# Revit family: Mailboxes_4C-Salsbury_Industries-Front_Load-Max_Height_Units
name_source: partatom
category: Specialty Equipment
revit_build: Autodesk Revit 2016 (Build: 20190507_1515(x64)
units: mm (PartAtom-declared; Revit-internal decimal feet)

## family parameters
Cut with Voids When Loaded = No
Host = Face
OmniClass Number = 23.40.90.14.11
OmniClass Title = Mail Boxes
Part Type = Normal
Room Calculation Point = No
Round Connector Dimension = Use Diameter
Shared = No

## types (12) — shared parameters
Assembly Code = C1030910
Assembly Description = Mailboxes
Back Enclosure Material = Aluminum Alloy - Salsbury Finish - Clear (No finish)
Center Divider Offset = 14.381"
Decals = Polycarbonate Film - Salsbury Finish - White
Depth = 16.450"
Door Depth = 0.190"
Height = 57.140"
Lock Material = Stainless Steel - Salsbury Finish -  Polished
Manufacturer = Salsbury Industries
MasterFormat Number = 10 55 00
MasterFormat Title = Postal Specialties
OmniClass 23 Number = 23.40.90.14.11
OmniClass 23 Title = Mail Boxes
Rough Opening - Height = 55.875"
URL = www.mailboxes.com
Version = 5.0 (01/01/21)

## per-type parameters (varying)
- 3716D-8P FL: Bottom Back Plate=Yes; Center Extrusion Offset=0.000"; Description=Max Height Unit: 2 PL3, 4 PL4, 2 PL4.5; Door Slot L1=3700 Series 4C Door Configurations : Empty; Door Slot L10=3700 Series 4C Door Configurations : Empty; Door Slot L10.5=3700 Series 4C Door Configurations : Empty; Door Slot L11=3700 Series 4C Parcel Configurations : PL4 w/ Divider; Door Slot L11.5=3700 Series 4C Door Configurations : Empty; Door Slot L12.5=3700 Series 4C Door Configurations : Empty; Door Slot L13.5=3700 Series 4C Door Configurations : Empty; Door Slot L16=3700 Series 4C Parcel Configurations : PL4.5 w/ Divider; Door Slot L2=3700 Series 4C Door Configurations : Empty; Door Slot L3=3700 Series 4C Parcel Configurations : PL3; Door Slot L4=3700 Series 4C Door Configurations : Empty; Door Slot L5=3700 Series 4C Door Configurations : Empty; Door Slot L6=3700 Series 4C Door Configurations : Empty; Door Slot L6.5=3700 Series 4C Door Configurations : Empty; Door Slot L7=3700 Series 4C Parcel Configurations : PL4 w/ Divider; Door Slot L7.5=3700 Series 4C Door Configurations : Empty; Door Slot L8=3700 Series 4C Door Configurations : Empty; Door Slot L8.5=3700 Series 4C Door Configurations : Empty; Door Slot L9=3700 Series 4C Door Configurations : Empty; Door Slot L9.5=3700 Series 4C Door Configurations : Empty; Door Slot R1=3700 Series 4C Door Configurations : Empty; Door Slot R10=3700 Series 4C Door Configurations : Empty; Door Slot R10.5=3700 Series 4C Door Configurations : Empty; Door Slot R11=3700 Series 4C Parcel Configurations : PL4 w/ Divider; Door Slot R11.5=3700 Series 4C Door Configurations : Empty; Door Slot R12.5=3700 Series 4C Door Configurations : Empty; Door Slot R13.5=3700 Series 4C Door Configurations : Empty; Door Slot R16=3700 Series 4C Parcel Configurations : PL4.5 w/ Divider; Door Slot R2=3700 Series 4C Door Configurations : Empty; Door Slot R3=3700 Series 4C Parcel Configurations : PL3; Door Slot R4=3700 Series 4C Door Configurations : Empty; Door Slot R5=3700 Series 4C Door Configurations : Empty; Door Slot R6=3700 Series 4C Door Configurations : Empty; Door Slot R6.5=3700 Series 4C Door Configurations : Empty; Door Slot R7=3700 Series 4C Parcel Configurations : PL4 w/ Divider; Door Slot R7.5=3700 Series 4C Door Configurations : Empty; Door Slot R8=3700 Series 4C Door Configurations : Empty; Door Slot R8.5=3700 Series 4C Door Configurations : Empty; Door Slot R9=3700 Series 4C Door Configurations : Empty; Door Slot R9.5=3700 Series 4C Door Configurations : Empty; Door Spacer=3700 Series 4C Door Configurations : Empty; Double Wide Hidden Components=Yes; Left Inside Wall=Yes; Right Inside Wall=Yes; Rough Opening - Width=29.875"; Top Back Plate=Yes; Type Comments=4C Standard Horizontal Mailbox - Front Loading; Vertical Center Divider=Yes; Width=31.097"
- 3716D-20 FL: Bottom Back Plate=Yes; Center Extrusion Offset=0.000"; Description=Max Height Unit: 20 MB1, 2 PL4.5, OM2; Door Slot L1=3700 Series 4C Door Configurations : MB1 Door; Door Slot L10=3700 Series 4C Door Configurations : MB1 Door w/ Divider; Door Slot L10.5=3700 Series 4C Door Configurations : Empty; Door Slot L11=3700 Series 4C Door Configurations : MB1 Door w/ Divider; Door Slot L11.5=3700 Series 4C Door Configurations : Empty; Door Slot L12.5=3700 Series 4C Door Configurations : Empty; Door Slot L13.5=3700 Series 4C Door Configurations : Empty; Door Slot L16=3700 Series 4C Parcel Configurations : PL4.5 w/ Divider; Door Slot L2=3700 Series 4C Door Configurations : MB1 Door w/ Divider; Door Slot L3=3700 Series 4C Door Configurations : MB1 Door w/ Divider; Door Slot L4=3700 Series 4C Door Configurations : MB1 Door w/ Divider; Door Slot L5=3700 Series 4C Door Configurations : MB1 Door w/ Divider; Door Slot L6=3700 Series 4C Door Configurations : MB1 Door w/ Divider; Door Slot L6.5=3700 Series 4C Door Configurations : Empty; Door Slot L7=3700 Series 4C Door Configurations : MB1 Door w/ Divider; Door Slot L7.5=3700 Series 4C Door Configurations : Empty; Door Slot L8=3700 Series 4C Door Configurations : MB1 Door w/ Divider; Door Slot L8.5=3700 Series 4C Door Configurations : Empty; Door Slot L9=3700 Series 4C Door Configurations : MB1 Door w/ Divider; Door Slot L9.5=3700 Series 4C Door Configurations : Empty; Door Slot R1=3700 Series 4C Door Configurations : MB1 Door; Door Slot R10=3700 Series 4C Door Configurations : MB1 Door w/ Divider; Door Slot R10.5=3700 Series 4C Door Configurations : Empty; Door Slot R11=3700 Series 4C Door Configurations : MB1 Door w/ Divider; Door Slot R11.5=3700 Series 4C Door Configurations : Empty; Door Slot R12.5=3700 Series 4C Door Configurations : Empty; Door Slot R13.5=3700 Series 4C Door Configurations : Empty; Door Slot R16=3700 Series 4C Parcel Configurations : PL4.5 w/ Divider; Door Slot R2=3700 Series 4C Door Configurations : MB1 Door w/ Divider; Door Slot R3=3700 Series 4C Door Configurations : MB1 Door w/ Divider; Door Slot R4=3700 Series 4C Door Configurations : MB1 Door w/ Divider; Door Slot R5=3700 Series 4C Door Configurations : MB1 Door w/ Divider; Door Slot R6=3700 Series 4C Door Configurations : MB1 Door w/ Divider; Door Slot R6.5=3700 Series 4C Door Configurations : Empty; Door Slot R7=3700 Series 4C Door Configurations : Empty; Door Slot R7.5=3700 Series 4C Door Configurations : Empty; Door Slot R8=3700 Series 4C OM2 Configuration : OM2-FL; Door Slot R8.5=3700 Series 4C Door Configurations : Empty; Door Slot R9=3700 Series 4C Door Configurations : MB1 Door w/ Divider; Door Slot R9.5=3700 Series 4C Door Configurations : Empty; Door Spacer=3700 Series 4C Door Configurations : Empty; Double Wide Hidden Components=Yes; Left Inside Wall=Yes; Right Inside Wall=Yes; Rough Opening - Width=29.875"; Top Back Plate=Yes; Type Comments=4C Standard Horizontal Mailbox - Front Loading; Vertical Center Divider=Yes; Width=31.097"
- 3716D-29 FL: Bottom Back Plate=Yes; Center Extrusion Offset=0.000"; Description=Max Height Unit: 29 MB1, OM1.5; Door Slot L1=3700 Series 4C Door Configurations : MB1 Door; Door Slot L10=3700 Series 4C Door Configurations : Empty; Door Slot L10.5=3700 Series 4C Door Configurations : MB1 Door w/ Divider; Door Slot L11=3700 Series 4C Door Configurations : Empty; Door Slot L11.5=3700 Series 4C Door Configurations : MB1 Door w/ Divider; Door Slot L12.5=3700 Series 4C Door Configurations : MB1 Door w/ Divider; Door Slot L13.5=3700 Series 4C Door Configurations : MB1 Door w/ Divider; Door Slot L16=3700 Series 4C Door Configurations : MB1 Door w/ Divider; Door Slot L2=3700 Series 4C Door Configurations : MB1 Door w/ Divider; Door Slot L3=3700 Series 4C Door Configurations : MB1 Door w/ Divider; Door Slot L4=3700 Series 4C Door Configurations : MB1 Door w/ Divider; Door Slot L5=3700 Series 4C Door Configurations : MB1 Door w/ Divider; Door Slot L6=3700 Series 4C Door Configurations : MB1 Door w/ Divider; Door Slot L6.5=3700 Series 4C Door Configurations : MB1 Door w/ Divider; Door Slot L7=3700 Series 4C Door Configurations : Empty; Door Slot L7.5=3700 Series 4C Door Configurations : MB1 Door w/ Divider; Door Slot L8=3700 Series 4C Door Configurations : Empty; Door Slot L8.5=3700 Series 4C Door Configurations : MB1 Door w/ Divider; Door Slot L9=3700 Series 4C Door Configurations : Empty; Door Slot L9.5=3700 Series 4C Door Configurations : MB1 Door w/ Divider; Door Slot R1=3700 Series 4C Door Configurations : MB1 Door; Door Slot R10=3700 Series 4C Door Configurations : Empty; Door Slot R10.5=3700 Series 4C Door Configurations : MB1 Door w/ Divider; Door Slot R11=3700 Series 4C Door Configurations : Empty; Door Slot R11.5=3700 Series 4C Door Configurations : MB1 Door w/ Divider; Door Slot R12.5=3700 Series 4C Door Configurations : MB1 Door w/ Divider; Door Slot R13.5=3700 Series 4C Door Configurations : MB1 Door w/ Divider; Door Slot R16=3700 Series 4C Door Configurations : MB1 Door w/ Divider; Door Slot R2=3700 Series 4C Door Configurations : MB1 Door w/ Divider; Door Slot R3=3700 Series 4C Door Configurations : MB1 Door w/ Divider; Door Slot R4=3700 Series 4C Door Configurations : MB1 Door w/ Divider; Door Slot R5=3700 Series 4C Door Configurations : MB1 Door w/ Divider; Door Slot R6=3700 Series 4C Door Configurations : MB1 Door w/ Divider; Door Slot R6.5=3700 Series 4C OM1.5 Configuration : OM1.5-FL; Door Slot R7=3700 Series 4C Door Configurations : Empty; Door Slot R7.5=3700 Series 4C Door Configurations : MB1 Door w/ Divider; Door Slot R8=3700 Series 4C Door Configurations : Empty; Door Slot R8.5=3700 Series 4C Door Configurations : MB1 Door w/ Divider; Door Slot R9=3700 Series 4C Door Configurations : Empty; Door Slot R9.5=3700 Series 4C Door Configurations : MB1 Door w/ Divider; Door Spacer=3700 Series 4C Door Spacing Filler : Door Space Filler; Double Wide Hidden Components=Yes; Left Inside Wall=Yes; Right Inside Wall=Yes; Rough Opening - Width=29.875"; Top Back Plate=Yes; Type Comments=4C Standard Horizontal Mailbox - Front Loading; Vertical Center Divider=Yes; Width=31.097"
- 3716S-06 FL: Bottom Back Plate=No; Center Extrusion Offset=0.350"; Description=Max Height Unit: 6 MB1, 1 PL3, 1 PL4.5, OM2; Door Slot L1=3700 Series 4C Door Configurations : Empty; Door Slot L10=3700 Series 4C Door Configurations : Empty; Door Slot L10.5=3700 Series 4C Door Configurations : Empty; Door Slot L11=3700 Series 4C Door Configurations : Empty; Door Slot L11.5=3700 Series 4C Door Configurations : Empty; Door Slot L12.5=3700 Series 4C Door Configurations : Empty; Door Slot L13.5=3700 Series 4C Door Configurations : Empty; Door Slot L16=3700 Series 4C Door Configurations : Empty; Door Slot L2=3700 Series 4C Door Configurations : Empty; Door Slot L3=3700 Series 4C Door Configurations : Empty; Door Slot L4=3700 Series 4C Door Configurations : Empty; Door Slot L5=3700 Series 4C Door Configurations : Empty; Door Slot L6=3700 Series 4C Door Configurations : Empty; Door Slot L6.5=3700 Series 4C Door Configurations : Empty; Door Slot L7=3700 Series 4C Door Configurations : Empty; Door Slot L7.5=3700 Series 4C Door Configurations : Empty; Door Slot L8=3700 Series 4C Door Configurations : Empty; Door Slot L8.5=3700 Series 4C Door Configurations : Empty; Door Slot L9=3700 Series 4C Door Configurations : Empty; Door Slot L9.5=3700 Series 4C Door Configurations : Empty; Door Slot R1=3700 Series 4C Door Configurations : MB1 Door; Door Slot R10=3700 Series 4C Door Configurations : Empty; Door Slot R10.5=3700 Series 4C Door Configurations : Empty; Door Slot R11=3700 Series 4C Parcel Configurations : PL3 w/ Divider; Door Slot R11.5=3700 Series 4C Door Configurations : Empty; Door Slot R12.5=3700 Series 4C Door Configurations : Empty; Door Slot R13.5=3700 Series 4C Door Configurations : Empty; Door Slot R16=3700 Series 4C Parcel Configurations : PL4.5 w/ Divider; Door Slot R2=3700 Series 4C Door Configurations : MB1 Door w/ Divider; Door Slot R3=3700 Series 4C Door Configurations : MB1 Door w/ Divider; Door Slot R4=3700 Series 4C Door Configurations : MB1 Door w/ Divider; Door Slot R5=3700 Series 4C Door Configurations : MB1 Door w/ Divider; Door Slot R6=3700 Series 4C Door Configurations : MB1 Door w/ Divider; Door Slot R6.5=3700 Series 4C Door Configurations : Empty; Door Slot R7=3700 Series 4C Door Configurations : Empty; Door Slot R7.5=3700 Series 4C Door Configurations : Empty; Door Slot R8=3700 Series 4C OM2 Configuration : OM2-FL; Door Slot R8.5=3700 Series 4C Door Configurations : Empty; Door Slot R9=3700 Series 4C Door Configurations : Empty; Door Slot R9.5=3700 Series 4C Door Configurations : Empty; Door Spacer=3700 Series 4C Door Configurations : Empty; Double Wide Hidden Components=No; Left Inside Wall=No; Right Inside Wall=No; Rough Opening - Width=15.750"; Top Back Plate=No; Type Comments=4C Standard Horizontal Mailbox - Front Loading; Vertical Center Divider=No; Width=16.966"
- 3716S-3P FL: Bottom Back Plate=No; Center Extrusion Offset=0.350"; Description=Max Height Unit: 1 PL4.5, 1 PL5, 1 PL6; Door Slot L1=3700 Series 4C Door Configurations : Empty; Door Slot L10=3700 Series 4C Door Configurations : Empty; Door Slot L10.5=3700 Series 4C Door Configurations : Empty; Door Slot L11=3700 Series 4C Door Configurations : Empty; Door Slot L11.5=3700 Series 4C Door Configurations : Empty; Door Slot L12.5=3700 Series 4C Door Configurations : Empty; Door Slot L13.5=3700 Series 4C Door Configurations : Empty; Door Slot L16=3700 Series 4C Door Configurations : Empty; Door Slot L2=3700 Series 4C Door Configurations : Empty; Door Slot L3=3700 Series 4C Door Configurations : Empty; Door Slot L4=3700 Series 4C Door Configurations : Empty; Door Slot L5=3700 Series 4C Door Configurations : Empty; Door Slot L6=3700 Series 4C Door Configurations : Empty; Door Slot L6.5=3700 Series 4C Door Configurations : Empty; Door Slot L7=3700 Series 4C Door Configurations : Empty; Door Slot L7.5=3700 Series 4C Door Configurations : Empty; Door Slot L8=3700 Series 4C Door Configurations : Empty; Door Slot L8.5=3700 Series 4C Door Configurations : Empty; Door Slot L9=3700 Series 4C Door Configurations : Empty; Door Slot L9.5=3700 Series 4C Door Configurations : Empty; Door Slot R1=3700 Series 4C Door Configurations : Empty; Door Slot R10=3700 Series 4C Door Configurations : Empty; Door Slot R10.5=3700 Series 4C Door Configurations : Empty; Door Slot R11=3700 Series 4C Parcel Configurations : PL6 w/ Divider; Door Slot R11.5=3700 Series 4C Door Configurations : Empty; Door Slot R12.5=3700 Series 4C Door Configurations : Empty; Door Slot R13.5=3700 Series 4C Door Configurations : Empty; Door Slot R16=3700 Series 4C Parcel Configurations : PL4.5 w/ Divider; Door Slot R2=3700 Series 4C Door Configurations : Empty; Door Slot R3=3700 Series 4C Door Configurations : Empty; Door Slot R4=3700 Series 4C Door Configurations : Empty; Door Slot R5=3700 Series 4C Parcel Configurations : PL5; Door Slot R6=3700 Series 4C Door Configurations : Empty; Door Slot R6.5=3700 Series 4C Door Configurations : Empty; Door Slot R7=3700 Series 4C Door Configurations : Empty; Door Slot R7.5=3700 Series 4C Door Configurations : Empty; Door Slot R8=3700 Series 4C Door Configurations : Empty; Door Slot R8.5=3700 Series 4C Door Configurations : Empty; Door Slot R9=3700 Series 4C Door Configurations : Empty; Door Slot R9.5=3700 Series 4C Door Configurations : Empty; Door Spacer=3700 Series 4C Door Configurations : Empty; Double Wide Hidden Components=No; Left Inside Wall=No; Right Inside Wall=No; Rough Opening - Width=15.750"; Top Back Plate=No; Type Comments=4C Standard Horizontal Mailbox - Front Loading; Vertical Center Divider=No; Width=16.966"
- 3716S-14 FL: Bottom Back Plate=No; Center Extrusion Offset=0.350"; Description=Max Height Unit: 14 MB1, OM2; Door Slot L1=3700 Series 4C Door Configurations : Empty; Door Slot L10=3700 Series 4C Door Configurations : Empty; Door Slot L10.5=3700 Series 4C Door Configurations : Empty; Door Slot L11=3700 Series 4C Door Configurations : Empty; Door Slot L11.5=3700 Series 4C Door Configurations : Empty; Door Slot L12.5=3700 Series 4C Door Configurations : Empty; Door Slot L13.5=3700 Series 4C Door Configurations : Empty; Door Slot L16=3700 Series 4C Door Configurations : Empty; Door Slot L2=3700 Series 4C Door Configurations : Empty; Door Slot L3=3700 Series 4C Door Configurations : Empty; Door Slot L4=3700 Series 4C Door Configurations : Empty; Door Slot L5=3700 Series 4C Door Configurations : Empty; Door Slot L6=3700 Series 4C Door Configurations : Empty; Door Slot L6.5=3700 Series 4C Door Configurations : Empty; Door Slot L7=3700 Series 4C Door Configurations : Empty; Door Slot L7.5=3700 Series 4C Door Configurations : Empty; Door Slot L8=3700 Series 4C Door Configurations : Empty; Door Slot L8.5=3700 Series 4C Door Configurations : Empty; Door Slot L9=3700 Series 4C Door Configurations : Empty; Door Slot L9.5=3700 Series 4C Door Configurations : Empty; Door Slot R1=3700 Series 4C Door Configurations : MB1 Door; Door Slot R10=3700 Series 4C Door Configurations : Empty; Door Slot R10.5=3700 Series 4C Door Configurations : MB1 Door w/ Divider; Door Slot R11=3700 Series 4C Door Configurations : Empty; Door Slot R11.5=3700 Series 4C Door Configurations : MB1 Door w/ Divider; Door Slot R12.5=3700 Series 4C Door Configurations : MB1 Door w/ Divider; Door Slot R13.5=3700 Series 4C Door Configurations : MB1 Door w/ Divider; Door Slot R16=3700 Series 4C Door Configurations : MB1 Door w/ Divider; Door Slot R2=3700 Series 4C Door Configurations : MB1 Door w/ Divider; Door Slot R3=3700 Series 4C Door Configurations : MB1 Door w/ Divider; Door Slot R4=3700 Series 4C Door Configurations : MB1 Door w/ Divider; Door Slot R5=3700 Series 4C Door Configurations : MB1 Door w/ Divider; Door Slot R6=3700 Series 4C Door Configurations : MB1 Door w/ Divider; Door Slot R6.5=3700 Series 4C OM1.5 Configuration : OM1.5-FL; Door Slot R7=3700 Series 4C Door Configurations : Empty; Door Slot R7.5=3700 Series 4C Door Configurations : MB1 Door w/ Divider; Door Slot R8=3700 Series 4C Door Configurations : Empty; Door Slot R8.5=3700 Series 4C Door Configurations : MB1 Door w/ Divider; Door Slot R9=3700 Series 4C Door Configurations : Empty; Door Slot R9.5=3700 Series 4C Door Configurations : MB1 Door w/ Divider; Door Spacer=3700 Series 4C Door Configurations : Empty; Double Wide Hidden Components=No; Left Inside Wall=No; Right Inside Wall=No; Rough Opening - Width=15.750"; Top Back Plate=No; Type Comments=4C Standard Horizontal Mailbox - Front Loading; Vertical Center Divider=No; Width=16.966"
- 3716S-09 FL: Bottom Back Plate=No; Center Extrusion Offset=0.350"; Description=Max Height Unit: 9 MB1, 1 PL4.5, OM2; Door Slot L1=3700 Series 4C Door Configurations : Empty; Door Slot L10=3700 Series 4C Door Configurations : Empty; Door Slot L10.5=3700 Series 4C Door Configurations : Empty; Door Slot L11=3700 Series 4C Door Configurations : Empty; Door Slot L11.5=3700 Series 4C Door Configurations : Empty; Door Slot L12.5=3700 Series 4C Door Configurations : Empty; Door Slot L13.5=3700 Series 4C Door Configurations : Empty; Door Slot L16=3700 Series 4C Door Configurations : Empty; Door Slot L2=3700 Series 4C Door Configurations : Empty; Door Slot L3=3700 Series 4C Door Configurations : Empty; Door Slot L4=3700 Series 4C Door Configurations : Empty; Door Slot L5=3700 Series 4C Door Configurations : Empty; Door Slot L6=3700 Series 4C Door Configurations : Empty; Door Slot L6.5=3700 Series 4C Door Configurations : Empty; Door Slot L7=3700 Series 4C Door Configurations : Empty; Door Slot L7.5=3700 Series 4C Door Configurations : Empty; Door Slot L8=3700 Series 4C Door Configurations : Empty; Door Slot L8.5=3700 Series 4C Door Configurations : Empty; Door Slot L9=3700 Series 4C Door Configurations : Empty; Door Slot L9.5=3700 Series 4C Door Configurations : Empty; Door Slot R1=3700 Series 4C Door Configurations : MB1 Door; Door Slot R10=3700 Series 4C Door Configurations : MB1 Door w/ Divider; Door Slot R10.5=3700 Series 4C Door Configurations : Empty; Door Slot R11=3700 Series 4C Door Configurations : MB1 Door w/ Divider; Door Slot R11.5=3700 Series 4C Door Configurations : Empty; Door Slot R12.5=3700 Series 4C Door Configurations : Empty; Door Slot R13.5=3700 Series 4C Door Configurations : Empty; Door Slot R16=3700 Series 4C Parcel Configurations : PL4.5 w/ Divider; Door Slot R2=3700 Series 4C Door Configurations : MB1 Door w/ Divider; Door Slot R3=3700 Series 4C Door Configurations : MB1 Door w/ Divider; Door Slot R4=3700 Series 4C Door Configurations : MB1 Door w/ Divider; Door Slot R5=3700 Series 4C Door Configurations : MB1 Door w/ Divider; Door Slot R6=3700 Series 4C Door Configurations : MB1 Door w/ Divider; Door Slot R6.5=3700 Series 4C Door Configurations : Empty; Door Slot R7=3700 Series 4C Door Configurations : Empty; Door Slot R7.5=3700 Series 4C Door Configurations : Empty; Door Slot R8=3700 Series 4C OM2 Configuration : OM2-FL; Door Slot R8.5=3700 Series 4C Door Configurations : Empty; Door Slot R9=3700 Series 4C Door Configurations : MB1 Door w/ Divider; Door Slot R9.5=3700 Series 4C Door Configurations : Empty; Door Spacer=3700 Series 4C Door Configurations : Empty; Double Wide Hidden Components=No; Left Inside Wall=No; Right Inside Wall=No; Rough Opening - Width=15.750"; Top Back Plate=No; Type Comments=4C Standard Horizontal Mailbox - Front Loading; Vertical Center Divider=No; Width=16.966"
- 3716S-2B FL: Bottom Back Plate=No; Center Extrusion Offset=0.350"; Description=Max Height Unit: 2 Receptacles; Door Slot L1=3700 Series 4C Door Configurations : Empty; Door Slot L10=3700 Series 4C Door Configurations : Empty; Door Slot L10.5=3700 Series 4C Door Configurations : Empty; Door Slot L11=3700 Series 4C Door Configurations : Empty; Door Slot L11.5=3700 Series 4C Door Configurations : Empty; Door Slot L12.5=3700 Series 4C Door Configurations : Empty; Door Slot L13.5=3700 Series 4C Door Configurations : Empty; Door Slot L16=3700 Series 4C Door Configurations : Empty; Door Slot L2=3700 Series 4C Door Configurations : Empty; Door Slot L3=3700 Series 4C Door Configurations : Empty; Door Slot L4=3700 Series 4C Door Configurations : Empty; Door Slot L5=3700 Series 4C Door Configurations : Empty; Door Slot L6=3700 Series 4C Door Configurations : Empty; Door Slot L6.5=3700 Series 4C Door Configurations : Empty; Door Slot L7=3700 Series 4C Door Configurations : Empty; Door Slot L7.5=3700 Series 4C Door Configurations : Empty; Door Slot L8=3700 Series 4C Door Configurations : Empty; Door Slot L8.5=3700 Series 4C Door Configurations : Empty; Door Slot L9=3700 Series 4C Door Configurations : Empty; Door Slot L9.5=3700 Series 4C Door Configurations : Empty; Door Slot R1=3700 Series 4C Door Configurations : Empty; Door Slot R10=3700 Series 4C Door Configurations : Empty; Door Slot R10.5=3700 Series 4C Door Configurations : Empty; Door Slot R11=3700 Series 4C Door Configurations : Empty; Door Slot R11.5=3700 Series 4C Door Configurations : Empty; Door Slot R12.5=3700 Series 4C Door Configurations : Empty; Door Slot R13.5=3700 Series 4C Door Configurations : Empty; Door Slot R16=4C-Max Height Receptacle; Door Slot R2=3700 Series 4C Door Configurations : Empty; Door Slot R3=3700 Series 4C Door Configurations : Empty; Door Slot R4=3700 Series 4C Door Configurations : Empty; Door Slot R5=3700 Series 4C Door Configurations : Empty; Door Slot R6=3700 Series 4C Door Configurations : Empty; Door Slot R6.5=3700 Series 4C Door Configurations : Empty; Door Slot R7=3700 Series 4C Door Configurations : Empty; Door Slot R7.5=3700 Series 4C Door Configurations : Empty; Door Slot R8=3700 Series 4C Door Configurations : Empty; Door Slot R8.5=3700 Series 4C Door Configurations : Empty; Door Slot R9=3700 Series 4C Door Configurations : Empty; Door Slot R9.5=3700 Series 4C Door Configurations : Empty; Door Spacer=3700 Series 4C Door Configurations : Empty; Double Wide Hidden Components=No; Left Inside Wall=No; Right Inside Wall=No; Rough Opening - Width=15.750"; Top Back Plate=No; Type Comments=4C Standard Horizontal Receptacle - Front Loading; Vertical Center Divider=No; Width=16.966"
- 3716S-1C FL: Bottom Back Plate=No; Center Extrusion Offset=0.350"; Description=Max Height Unit: 1 Collection Box; Door Slot L1=3700 Series 4C Door Configurations : Empty; Door Slot L10=3700 Series 4C Door Configurations : Empty; Door Slot L10.5=3700 Series 4C Door Configurations : Empty; Door Slot L11=3700 Series 4C Door Configurations : Empty; Door Slot L11.5=3700 Series 4C Door Configurations : Empty; Door Slot L12.5=3700 Series 4C Door Configurations : Empty; Door Slot L13.5=3700 Series 4C Door Configurations : Empty; Door Slot L16=3700 Series 4C Door Configurations : Empty; Door Slot L2=3700 Series 4C Door Configurations : Empty; Door Slot L3=3700 Series 4C Door Configurations : Empty; Door Slot L4=3700 Series 4C Door Configurations : Empty; Door Slot L5=3700 Series 4C Door Configurations : Empty; Door Slot L6=3700 Series 4C Door Configurations : Empty; Door Slot L6.5=3700 Series 4C Door Configurations : Empty; Door Slot L7=3700 Series 4C Door Configurations : Empty; Door Slot L7.5=3700 Series 4C Door Configurations : Empty; Door Slot L8=3700 Series 4C Door Configurations : Empty; Door Slot L8.5=3700 Series 4C Door Configurations : Empty; Door Slot L9=3700 Series 4C Door Configurations : Empty; Door Slot L9.5=3700 Series 4C Door Configurations : Empty; Door Slot R1=3700 Series 4C Door Configurations : Empty; Door Slot R10=3700 Series 4C Door Configurations : Empty; Door Slot R10.5=3700 Series 4C Door Configurations : Empty; Door Slot R11=3700 Series 4C Door Configurations : Empty; Door Slot R11.5=3700 Series 4C Door Configurations : Empty; Door Slot R12.5=3700 Series 4C Door Configurations : Empty; Door Slot R13.5=3700 Series 4C Door Configurations : Empty; Door Slot R16=4C-Max Height Collection Box; Door Slot R2=3700 Series 4C Door Configurations : Empty; Door Slot R3=3700 Series 4C Door Configurations : Empty; Door Slot R4=3700 Series 4C Door Configurations : Empty; Door Slot R5=3700 Series 4C Door Configurations : Empty; Door Slot R6=3700 Series 4C Door Configurations : Empty; Door Slot R6.5=3700 Series 4C Door Configurations : Empty; Door Slot R7=3700 Series 4C Door Configurations : Empty; Door Slot R7.5=3700 Series 4C Door Configurations : Empty; Door Slot R8=3700 Series 4C Door Configurations : Empty; Door Slot R8.5=3700 Series 4C Door Configurations : Empty; Door Slot R9=3700 Series 4C Door Configurations : Empty; Door Slot R9.5=3700 Series 4C Door Configurations : Empty; Door Spacer=3700 Series 4C Door Configurations : Empty; Double Wide Hidden Components=No; Left Inside Wall=No; Right Inside Wall=No; Rough Opening - Width=15.750"; Top Back Plate=No; Type Comments=4C Standard Horizontal Receptacle - Front Loading; Vertical Center Divider=No; Width=16.966"
- 3716D-15 FL: Bottom Back Plate=Yes; Center Extrusion Offset=0.000"; Description=Max Height Unit: 15 MB1, 2 PL4.5, 1 PL5, OM2; Door Slot L1=3700 Series 4C Door Configurations : MB1 Door; Door Slot L10=3700 Series 4C Door Configurations : Empty; Door Slot L10.5=3700 Series 4C Door Configurations : Empty; Door Slot L11=3700 Series 4C Parcel Configurations : PL5 w/ Divider; Door Slot L11.5=3700 Series 4C Door Configurations : Empty; Door Slot L12.5=3700 Series 4C Door Configurations : Empty; Door Slot L13.5=3700 Series 4C Door Configurations : Empty; Door Slot L16=3700 Series 4C Parcel Configurations : PL4.5 w/ Divider; Door Slot L2=3700 Series 4C Door Configurations : MB1 Door w/ Divider; Door Slot L3=3700 Series 4C Door Configurations : MB1 Door w/ Divider; Door Slot L4=3700 Series 4C Door Configurations : MB1 Door w/ Divider; Door Slot L5=3700 Series 4C Door Configurations : MB1 Door w/ Divider; Door Slot L6=3700 Series 4C Door Configurations : MB1 Door w/ Divider; Door Slot L6.5=3700 Series 4C Door Configurations : Empty; Door Slot L7=3700 Series 4C Door Configurations : Empty; Door Slot L7.5=3700 Series 4C Door Configurations : Empty; Door Slot L8=3700 Series 4C Door Configurations : Empty; Door Slot L8.5=3700 Series 4C Door Configurations : Empty; Door Slot L9=3700 Series 4C Door Configurations : Empty; Door Slot L9.5=3700 Series 4C Door Configurations : Empty; Door Slot R1=3700 Series 4C Door Configurations : MB1 Door; Door Slot R10=3700 Series 4C Door Configurations : MB1 Door w/ Divider; Door Slot R10.5=3700 Series 4C Door Configurations : Empty; Door Slot R11=3700 Series 4C Door Configurations : MB1 Door w/ Divider; Door Slot R11.5=3700 Series 4C Door Configurations : Empty; Door Slot R12.5=3700 Series 4C Door Configurations : Empty; Door Slot R13.5=3700 Series 4C Door Configurations : Empty; Door Slot R16=3700 Series 4C Parcel Configurations : PL4.5 w/ Divider; Door Slot R2=3700 Series 4C Door Configurations : MB1 Door w/ Divider; Door Slot R3=3700 Series 4C Door Configurations : MB1 Door w/ Divider; Door Slot R4=3700 Series 4C Door Configurations : MB1 Door w/ Divider; Door Slot R5=3700 Series 4C Door Configurations : MB1 Door w/ Divider; Door Slot R6=3700 Series 4C Door Configurations : MB1 Door w/ Divider; Door Slot R6.5=3700 Series 4C Door Configurations : Empty; Door Slot R7=3700 Series 4C Door Configurations : Empty; Door Slot R7.5=3700 Series 4C Door Configurations : Empty; Door Slot R8=3700 Series 4C OM2 Configuration : OM2-FL; Door Slot R8.5=3700 Series 4C Door Configurations : Empty; Door Slot R9=3700 Series 4C Door Configurations : MB1 Door w/ Divider; Door Slot R9.5=3700 Series 4C Door Configurations : Empty; Door Spacer=3700 Series 4C Door Configurations : Empty; Double Wide Hidden Components=Yes; Left Inside Wall=Yes; Right Inside Wall=Yes; Rough Opening - Width=29.875"; Top Back Plate=Yes; Type Comments=4C Standard Horizontal Mailbox - Front Loading; Vertical Center Divider=Yes; Width=31.097"
- 3716D-10 FL: Bottom Back Plate=Yes; Center Extrusion Offset=0.000"; Description=Max Height Unit: 10 MB1, 2 PL4.5, 2 PL5, OM2; Door Slot L1=3700 Series 4C Door Configurations : MB1 Door; Door Slot L10=3700 Series 4C Door Configurations : Empty; Door Slot L10.5=3700 Series 4C Door Configurations : Empty; Door Slot L11=3700 Series 4C Parcel Configurations : PL5 w/ Divider; Door Slot L11.5=3700 Series 4C Door Configurations : Empty; Door Slot L12.5=3700 Series 4C Door Configurations : Empty; Door Slot L13.5=3700 Series 4C Door Configurations : Empty; Door Slot L16=3700 Series 4C Parcel Configurations : PL4.5 w/ Divider; Door Slot L2=3700 Series 4C Door Configurations : Empty; Door Slot L3=3700 Series 4C Door Configurations : Empty; Door Slot L4=3700 Series 4C Door Configurations : Empty; Door Slot L5=3700 Series 4C Door Configurations : Empty; Door Slot L6=3700 Series 4C Parcel Configurations : PL5 w/ Divider; Door Slot L6.5=3700 Series 4C Door Configurations : Empty; Door Slot L7=3700 Series 4C Door Configurations : Empty; Door Slot L7.5=3700 Series 4C Door Configurations : Empty; Door Slot L8=3700 Series 4C Door Configurations : Empty; Door Slot L8.5=3700 Series 4C Door Configurations : Empty; Door Slot L9=3700 Series 4C Door Configurations : Empty; Door Slot L9.5=3700 Series 4C Door Configurations : Empty; Door Slot R1=3700 Series 4C Door Configurations : MB1 Door; Door Slot R10=3700 Series 4C Door Configurations : MB1 Door w/ Divider; Door Slot R10.5=3700 Series 4C Door Configurations : Empty; Door Slot R11=3700 Series 4C Door Configurations : MB1 Door w/ Divider; Door Slot R11.5=3700 Series 4C Door Configurations : Empty; Door Slot R12.5=3700 Series 4C Door Configurations : Empty; Door Slot R13.5=3700 Series 4C Door Configurations : Empty; Door Slot R16=3700 Series 4C Parcel Configurations : PL4.5 w/ Divider; Door Slot R2=3700 Series 4C Door Configurations : MB1 Door w/ Divider; Door Slot R3=3700 Series 4C Door Configurations : MB1 Door w/ Divider; Door Slot R4=3700 Series 4C Door Configurations : MB1 Door w/ Divider; Door Slot R5=3700 Series 4C Door Configurations : MB1 Door w/ Divider; Door Slot R6=3700 Series 4C Door Configurations : MB1 Door w/ Divider; Door Slot R6.5=3700 Series 4C Door Configurations : Empty; Door Slot R7=3700 Series 4C Door Configurations : Empty; Door Slot R7.5=3700 Series 4C Door Configurations : Empty; Door Slot R8=3700 Series 4C OM2 Configuration : OM2-FL; Door Slot R8.5=3700 Series 4C Door Configurations : Empty; Door Slot R9=3700 Series 4C Door Configurations : MB1 Door w/ Divider; Door Slot R9.5=3700 Series 4C Door Configurations : Empty; Door Spacer=3700 Series 4C Door Configurations : Empty; Double Wide Hidden Components=Yes; Left Inside Wall=Yes; Right Inside Wall=Yes; Rough Opening - Width=29.875"; Top Back Plate=Yes; Type Comments=4C Standard Horizontal Mailbox - Front Loading; Vertical Center Divider=Yes; Width=31.097"
- 3716D-6P FL: Bottom Back Plate=Yes; Center Extrusion Offset=0.000"; Description=Max Height Unit: 2 PL4.5, 2 PL5, 2 PL6; Door Slot L1=3700 Series 4C Door Configurations : Empty; Door Slot L10=3700 Series 4C Door Configurations : Empty; Door Slot L10.5=3700 Series 4C Door Configurations : Empty; Door Slot L11=3700 Series 4C Parcel Configurations : PL6 w/ Divider; Door Slot L11.5=3700 Series 4C Door Configurations : Empty; Door Slot L12.5=3700 Series 4C Door Configurations : Empty; Door Slot L13.5=3700 Series 4C Door Configurations : Empty; Door Slot L16=3700 Series 4C Parcel Configurations : PL4.5 w/ Divider; Door Slot L2=3700 Series 4C Door Configurations : Empty; Door Slot L3=3700 Series 4C Door Configurations : Empty; Door Slot L4=3700 Series 4C Door Configurations : Empty; Door Slot L5=3700 Series 4C Parcel Configurations : PL5; Door Slot L6=3700 Series 4C Door Configurations : Empty; Door Slot L6.5=3700 Series 4C Door Configurations : Empty; Door Slot L7=3700 Series 4C Door Configurations : Empty; Door Slot L7.5=3700 Series 4C Door Configurations : Empty; Door Slot L8=3700 Series 4C Door Configurations : Empty; Door Slot L8.5=3700 Series 4C Door Configurations : Empty; Door Slot L9=3700 Series 4C Door Configurations : Empty; Door Slot L9.5=3700 Series 4C Door Configurations : Empty; Door Slot R1=3700 Series 4C Door Configurations : Empty; Door Slot R10=3700 Series 4C Door Configurations : Empty; Door Slot R10.5=3700 Series 4C Door Configurations : Empty; Door Slot R11=3700 Series 4C Parcel Configurations : PL6 w/ Divider; Door Slot R11.5=3700 Series 4C Door Configurations : Empty; Door Slot R12.5=3700 Series 4C Door Configurations : Empty; Door Slot R13.5=3700 Series 4C Door Configurations : Empty; Door Slot R16=3700 Series 4C Parcel Configurations : PL4.5 w/ Divider; Door Slot R2=3700 Series 4C Door Configurations : Empty; Door Slot R3=3700 Series 4C Door Configurations : Empty; Door Slot R4=3700 Series 4C Door Configurations : Empty; Door Slot R5=3700 Series 4C Parcel Configurations : PL5; Door Slot R6=3700 Series 4C Door Configurations : Empty; Door Slot R6.5=3700 Series 4C Door Configurations : Empty; Door Slot R7=3700 Series 4C Door Configurations : Empty; Door Slot R7.5=3700 Series 4C Door Configurations : Empty; Door Slot R8=3700 Series 4C Door Configurations : Empty; Door Slot R8.5=3700 Series 4C Door Configurations : Empty; Door Slot R9=3700 Series 4C Door Configurations : Empty; Door Slot R9.5=3700 Series 4C Door Configurations : Empty; Door Spacer=3700 Series 4C Door Configurations : Empty; Double Wide Hidden Components=Yes; Left Inside Wall=Yes; Right Inside Wall=Yes; Rough Opening - Width=29.875"; Top Back Plate=Yes; Type Comments=4C Standard Horizontal Mailbox - Front Loading; Vertical Center Divider=Yes; Width=31.097"

note: column(s) folded — value = type name in every type: Model

## geometry (parser evidence)
native form markers: Blend x6, Extrusion x4, Sweep x45
no freeform markers — native parametric forms only
